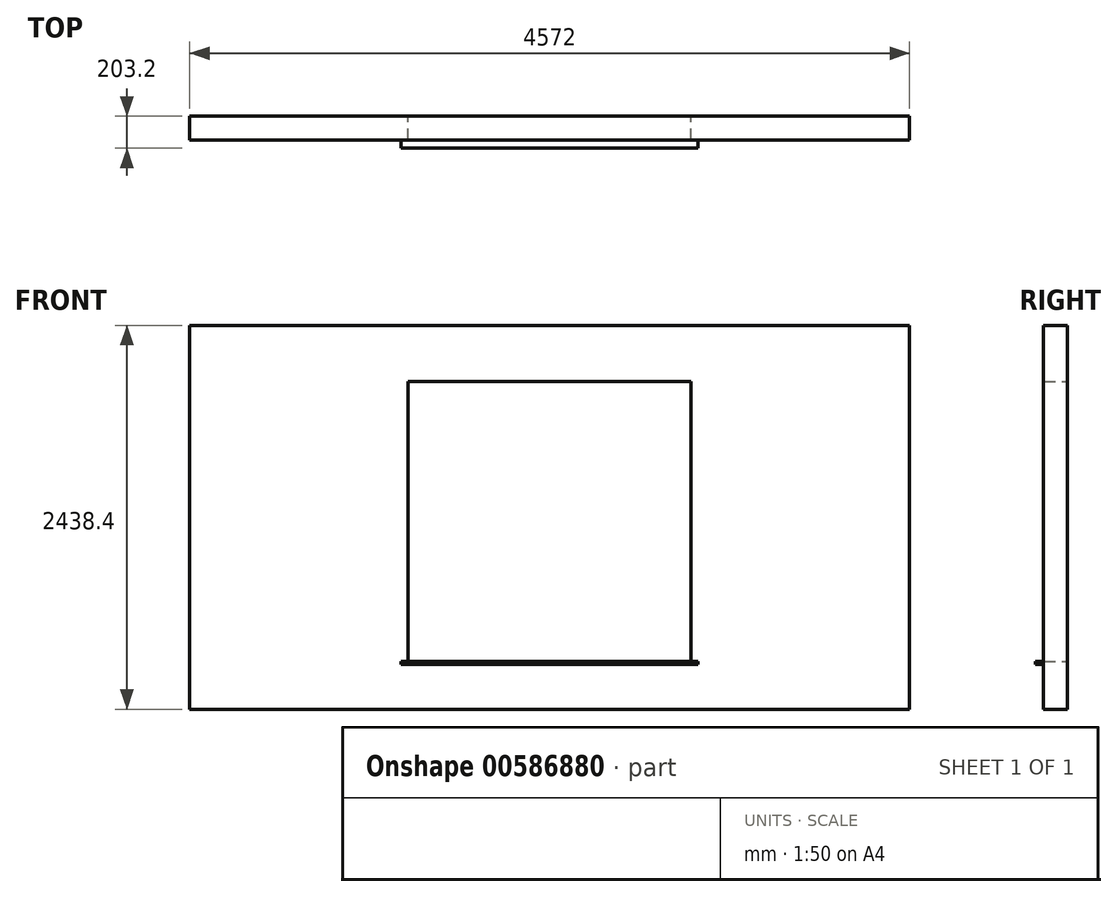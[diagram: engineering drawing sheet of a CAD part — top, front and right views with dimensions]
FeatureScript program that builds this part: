
annotation { "Feature Type Name" : "Feature", "Feature Type Description" : "" }
export const myFeature = defineFeature(function(context is Context, id is Id, definition is map)
    precondition{}
    {
        {
            var Q0;
            Q0=qCreatedBy(makeId("Front.planeOp"),FACE);
            var sketch = newSketch(context, id + "F0", { "sketchPlane" : qUnion([Q0])});
            skLineSegment(sketch, "E0.bottom", {"start": v(898.53, 863.6) * mm, "end": v(-898.53, 863.6) * mm});
            skLineSegment(sketch, "E0.top", {"start": v(898.53, -914.4) * mm, "end": v(-898.53, -914.4) * mm});
            skLineSegment(sketch, "E0.left", {"start": v(898.53, 863.6) * mm, "end": v(898.53, -914.4) * mm});
            skLineSegment(sketch, "E0.right", {"start": v(-898.53, 863.6) * mm, "end": v(-898.53, -914.4) * mm});
            skPoint(sketch, "E0.middle", {"position": v(0, -25.4) * mm});
            skLineSegment(sketch, "E1.bottom", {"start": v(2286, 1219.2) * mm, "end": v(-2286, 1219.2) * mm});
            skLineSegment(sketch, "E1.top", {"start": v(2286, -1219.2) * mm, "end": v(-2286, -1219.2) * mm});
            skLineSegment(sketch, "E1.left", {"start": v(2286, 1219.2) * mm, "end": v(2286, -1219.2) * mm});
            skLineSegment(sketch, "E1.right", {"start": v(-2286, 1219.2) * mm, "end": v(-2286, -1219.2) * mm});
            skPoint(sketch, "E1.middle", {"position": v(0, 0) * mm});
            skSolve(sketch);
        }
        {
            var Q0;
            Q0=makeQuery(id+"F0.imprint","IMPRINT",FACE,{"disambiguationData":[TD([[makeQuery(id+"F0.imprint","IMPRINT",EDGE,{"derivedFrom":sQuery(id+"F0.wireOp",EDGE,"E0.bottom")}),-1.0]])]});
            extrude(context, id + "F1", {"entities" : qUnion([Q0]), "depth" : 152.4 * mm, "offsetDistance" : 25.4 * mm});
        }
        {
            var Q0;
            Q0=makeQuery(id+"F1.opExtrude","SWEPT_FACE",FACE,{"disambiguationData":[OSD([sQuery(id+"F0.wireOp",EDGE,"E0.top")])]});
            var sketch = newSketch(context, id + "F2", { "sketchPlane" : qUnion([Q0])});
            skLineSegment(sketch, "E2.bottom", {"start": v(-942.98, -152.4) * mm, "end": v(942.98, -152.4) * mm});
            skLineSegment(sketch, "E2.top", {"start": v(-942.98, -203.2) * mm, "end": v(942.98, -203.2) * mm});
            skLineSegment(sketch, "E2.left", {"start": v(-942.98, -152.4) * mm, "end": v(-942.98, -203.2) * mm});
            skLineSegment(sketch, "E2.right", {"start": v(942.98, -152.4) * mm, "end": v(942.98, -203.2) * mm});
            skSolve(sketch);
        }
        {
            var Q0;
            Q0 = qSketchRegion(id + "F2", true);
            extrude(context, id + "F3", {"entities" : qUnion([Q0]), "operationType" : NewBodyOperationType.ADD, "oppositeDirection" : true, "depth" : 19.05 * mm, "offsetDistance" : 25.4 * mm});
        }
    });
